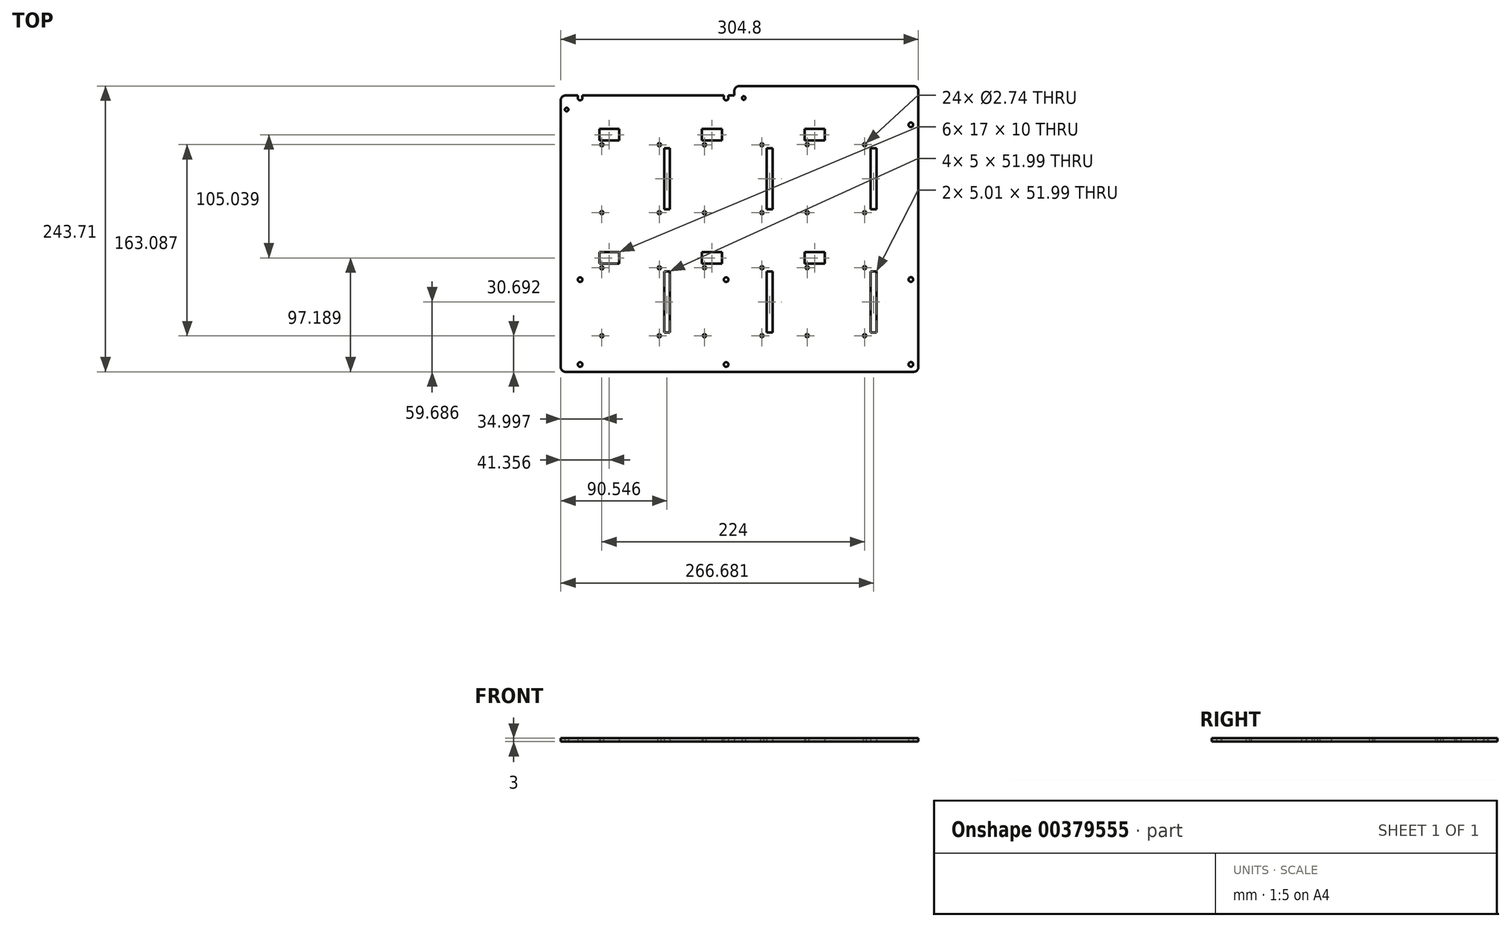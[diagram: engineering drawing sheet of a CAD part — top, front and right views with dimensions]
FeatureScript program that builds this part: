
annotation { "Feature Type Name" : "Feature", "Feature Type Description" : "" }
export const myFeature = defineFeature(function(context is Context, id is Id, definition is map)
    precondition{}
    {
        {
            var Q0;
            Q0=qCreatedBy(makeId("Top.planeOp"),FACE);
            var sketch = newSketch(context, id + "F0", { "sketchPlane" : qUnion([Q0])});
            skLineSegment(sketch, "E0.bottom", {"start": v(-157.61, -121.94) * mm, "end": v(139.26, -121.94) * mm});
            skLineSegment(sketch, "E0.top", {"start": v(-157.61, 121.77) * mm, "end": v(-156.57, 121.77) * mm});
            skLineSegment(sketch, "E0.left", {"start": v(-161.57, -117.98) * mm, "end": v(-161.57, 109.8) * mm});
            skLineSegment(sketch, "E0.right", {"start": v(143.23, -117.98) * mm, "end": v(143.23, 117.8) * mm});
            skArc(sketch, "E1", {"start": v(-147.04, 111.6) * mm, "mid": v(-145.06, 109.63) * mm, "end": v(-143.08, 111.6) * mm});
            skCircle(sketch, "E2", {"center": v(-145.06, -115.72) * mm, "radius": 1.98 * mm});
            skCircle(sketch, "E3", {"center": v(-145.06, -43.33) * mm, "radius": 1.98 * mm});
            skCircle(sketch, "E4", {"center": v(-20.6, -115.72) * mm, "radius": 1.98 * mm});
            skArc(sketch, "E5", {"start": v(-22.58, 111.6) * mm, "mid": v(-20.6, 109.63) * mm, "end": v(-18.62, 111.6) * mm});
            skCircle(sketch, "E6", {"center": v(136.88, 88.75) * mm, "radius": 1.98 * mm});
            skCircle(sketch, "E7", {"center": v(136.88, -115.6) * mm, "radius": 1.98 * mm});
            skCircle(sketch, "E8", {"center": v(136.88, -43.2) * mm, "radius": 1.98 * mm});
            skPoint(sketch, "E9.visualSharp", {"position": v(-161.57, 121.77) * mm});
            skPoint(sketch, "E10.visualSharp", {"position": v(-161.57, -121.94) * mm});
            skArc(sketch, "E10.filletArc", {"start": v(-161.57, -117.98) * mm, "mid": v(-160.41, -120.78) * mm, "end": v(-157.61, -121.94) * mm});
            skPoint(sketch, "E11.visualSharp", {"position": v(143.23, -121.94) * mm});
            skArc(sketch, "E11.filletArc", {"start": v(139.26, -121.94) * mm, "mid": v(142.07, -120.78) * mm, "end": v(143.23, -117.98) * mm});
            skPoint(sketch, "E12.visualSharp", {"position": v(143.23, 121.77) * mm});
            skArc(sketch, "E12.filletArc", {"start": v(143.23, 117.8) * mm, "mid": v(142.07, 120.6) * mm, "end": v(139.26, 121.77) * mm});
            skCircle(sketch, "E13.MirrorC", {"center": v(-77.58, 13.8) * mm, "radius": 1.37 * mm});
            skCircle(sketch, "E14.MirrorC", {"center": v(-126.57, 71.78) * mm, "radius": 1.37 * mm});
            skCircle(sketch, "E15.MirrorC", {"center": v(-126.57, 13.8) * mm, "radius": 1.37 * mm});
            skCircle(sketch, "E16.MirrorC", {"center": v(-77.58, 71.78) * mm, "radius": 1.37 * mm});
            skCircle(sketch, "E17.MirrorC", {"center": v(-77.58, -91.25) * mm, "radius": 1.37 * mm});
            skCircle(sketch, "E18.MirrorC", {"center": v(-126.57, -33.26) * mm, "radius": 1.37 * mm});
            skCircle(sketch, "E19.MirrorC", {"center": v(-77.58, -33.26) * mm, "radius": 1.37 * mm});
            skCircle(sketch, "E20.MirrorC", {"center": v(-126.57, -91.25) * mm, "radius": 1.37 * mm});
            skCircle(sketch, "E21.MirrorC", {"center": v(9.93, 13.75) * mm, "radius": 1.37 * mm});
            skCircle(sketch, "E22.MirrorC", {"center": v(-39.07, 71.73) * mm, "radius": 1.37 * mm});
            skCircle(sketch, "E23.MirrorC", {"center": v(-39.07, 13.75) * mm, "radius": 1.37 * mm});
            skCircle(sketch, "E24.MirrorC", {"center": v(9.93, 71.73) * mm, "radius": 1.37 * mm});
            skCircle(sketch, "E25.MirrorC", {"center": v(9.93, -91.12) * mm, "radius": 1.37 * mm});
            skCircle(sketch, "E26.MirrorC", {"center": v(-39.07, -33.14) * mm, "radius": 1.37 * mm});
            skCircle(sketch, "E27.MirrorC", {"center": v(9.93, -33.14) * mm, "radius": 1.37 * mm});
            skCircle(sketch, "E28.MirrorC", {"center": v(-39.07, -91.12) * mm, "radius": 1.37 * mm});
            skCircle(sketch, "E29.MirrorC", {"center": v(97.43, 13.85) * mm, "radius": 1.37 * mm});
            skCircle(sketch, "E30.MirrorC", {"center": v(48.43, 71.84) * mm, "radius": 1.37 * mm});
            skCircle(sketch, "E31.MirrorC", {"center": v(48.43, 13.85) * mm, "radius": 1.37 * mm});
            skCircle(sketch, "E32.MirrorC", {"center": v(97.43, 71.84) * mm, "radius": 1.37 * mm});
            skCircle(sketch, "E33.MirrorC", {"center": v(97.43, -91.1) * mm, "radius": 1.37 * mm});
            skCircle(sketch, "E34.MirrorC", {"center": v(48.43, -33.12) * mm, "radius": 1.37 * mm});
            skCircle(sketch, "E35.MirrorC", {"center": v(97.43, -33.12) * mm, "radius": 1.37 * mm});
            skCircle(sketch, "E36.MirrorC", {"center": v(48.43, -91.1) * mm, "radius": 1.37 * mm});
            skLineSegment(sketch, "E37.bottom", {"start": v(-128.71, -19.75) * mm, "end": v(-111.71, -19.75) * mm});
            skLineSegment(sketch, "E37.top", {"start": v(-128.71, -29.75) * mm, "end": v(-111.71, -29.75) * mm});
            skLineSegment(sketch, "E37.left", {"start": v(-128.71, -19.75) * mm, "end": v(-128.71, -29.75) * mm});
            skLineSegment(sketch, "E37.right", {"start": v(-41.2, -19.75) * mm, "end": v(-41.2, -29.75) * mm});
            skLineSegment(sketch, "E38.MirrorCS", {"start": v(-24.2, -19.75) * mm, "end": v(-24.2, -29.75) * mm});
            skLineSegment(sketch, "E39.MirrorCS", {"start": v(-24.2, -29.75) * mm, "end": v(-41.2, -29.75) * mm});
            skLineSegment(sketch, "E40.MirrorCS", {"start": v(-24.2, -19.75) * mm, "end": v(-41.2, -19.75) * mm});
            skLineSegment(sketch, "E41", {"start": v(-111.71, -19.75) * mm, "end": v(-111.71, -29.75) * mm});
            skLineSegment(sketch, "E42.right", {"start": v(46.3, -19.75) * mm, "end": v(46.3, -29.75) * mm});
            skLineSegment(sketch, "E43.MirrorCS", {"start": v(63.3, -19.75) * mm, "end": v(63.3, -29.75) * mm});
            skLineSegment(sketch, "E44.MirrorCS", {"start": v(63.3, -29.75) * mm, "end": v(46.3, -29.75) * mm});
            skLineSegment(sketch, "E45.MirrorCS", {"start": v(63.3, -19.75) * mm, "end": v(46.3, -19.75) * mm});
            skLineSegment(sketch, "E46.bottom", {"start": v(-73.52, 68.78) * mm, "end": v(-68.52, 68.78) * mm});
            skLineSegment(sketch, "E46.top", {"start": v(-73.52, 16.8) * mm, "end": v(-68.52, 16.8) * mm});
            skLineSegment(sketch, "E46.left", {"start": v(-73.52, 68.78) * mm, "end": v(-73.52, 16.8) * mm});
            skLineSegment(sketch, "E46.right", {"start": v(-68.52, 68.78) * mm, "end": v(-68.52, 16.8) * mm});
            skLineSegment(sketch, "E47.bottom", {"start": v(13.98, 68.78) * mm, "end": v(18.98, 68.78) * mm});
            skLineSegment(sketch, "E47.top", {"start": v(13.98, 16.8) * mm, "end": v(18.98, 16.8) * mm});
            skLineSegment(sketch, "E47.left", {"start": v(13.98, 68.78) * mm, "end": v(13.98, 16.8) * mm});
            skLineSegment(sketch, "E47.right", {"start": v(18.98, 68.78) * mm, "end": v(18.98, 16.8) * mm});
            skLineSegment(sketch, "E48.bottom", {"start": v(102.6, 68.78) * mm, "end": v(107.61, 68.78) * mm});
            skLineSegment(sketch, "E48.top", {"start": v(102.6, 16.8) * mm, "end": v(107.61, 16.8) * mm});
            skLineSegment(sketch, "E48.left", {"start": v(102.6, 68.78) * mm, "end": v(102.6, 16.8) * mm});
            skLineSegment(sketch, "E48.right", {"start": v(107.61, 68.78) * mm, "end": v(107.61, 16.8) * mm});
            skLineSegment(sketch, "E49.bottom", {"start": v(-73.52, -36.26) * mm, "end": v(-68.52, -36.26) * mm});
            skLineSegment(sketch, "E49.top", {"start": v(-73.52, -88.25) * mm, "end": v(-68.52, -88.25) * mm});
            skLineSegment(sketch, "E49.left", {"start": v(-73.52, -36.26) * mm, "end": v(-73.52, -88.25) * mm});
            skLineSegment(sketch, "E49.right", {"start": v(-68.52, -36.26) * mm, "end": v(-68.52, -88.25) * mm});
            skLineSegment(sketch, "E50.bottom", {"start": v(13.98, -36.26) * mm, "end": v(18.98, -36.26) * mm});
            skLineSegment(sketch, "E50.top", {"start": v(13.98, -88.25) * mm, "end": v(18.98, -88.25) * mm});
            skLineSegment(sketch, "E50.left", {"start": v(13.98, -36.26) * mm, "end": v(13.98, -88.25) * mm});
            skLineSegment(sketch, "E50.right", {"start": v(18.98, -36.26) * mm, "end": v(18.98, -88.25) * mm});
            skLineSegment(sketch, "E51.bottom", {"start": v(102.6, -36.26) * mm, "end": v(107.61, -36.26) * mm});
            skLineSegment(sketch, "E51.top", {"start": v(102.6, -88.25) * mm, "end": v(107.61, -88.25) * mm});
            skLineSegment(sketch, "E51.left", {"start": v(102.6, -36.26) * mm, "end": v(102.6, -88.25) * mm});
            skLineSegment(sketch, "E51.right", {"start": v(107.61, -36.26) * mm, "end": v(107.61, -88.25) * mm});
            skLineSegment(sketch, "E52", {"start": v(-242.67, -151.94) * mm, "end": v(205.36, -151.94) * mm, "construction": true});
            skCircle(sketch, "E53.MirrorC", {"center": v(-20.6, -43.33) * mm, "radius": 1.98 * mm});
            skLineSegment(sketch, "E54", {"start": v(-171.72, 113.77) * mm, "end": v(-147.04, 113.77) * mm, "construction": true});
            skLineSegment(sketch, "E55", {"start": v(-13.6, 137.69) * mm, "end": v(-13.6, 102.93) * mm, "construction": true});
            skLineSegment(sketch, "E56", {"start": v(-169.38, 111.6) * mm, "end": v(164.1, 111.6) * mm, "construction": true});
            skLineSegment(sketch, "E57", {"start": v(-5.6, 125.2) * mm, "end": v(-5.6, 95.42) * mm, "construction": true});
            skCircle(sketch, "E58", {"center": v(-5.6, 111.6) * mm, "radius": 1.5 * mm});
            skLineSegment(sketch, "E59", {"start": v(-156.57, 127.39) * mm, "end": v(-156.57, 85.38) * mm, "construction": true});
            skLineSegment(sketch, "E60", {"start": v(-167.89, 101.77) * mm, "end": v(-140.58, 101.77) * mm, "construction": true});
            skCircle(sketch, "E61", {"center": v(-156.57, 101.77) * mm, "radius": 1.5 * mm});
            skLineSegment(sketch, "E62", {"start": v(-157.61, 113.77) * mm, "end": v(-147.04, 113.77) * mm});
            skLineSegment(sketch, "E63", {"start": v(-13.6, 117.8) * mm, "end": v(-13.6, 117.8) * mm});
            skLineSegment(sketch, "E64.trimOffspring", {"start": v(-9.64, 121.77) * mm, "end": v(139.26, 121.77) * mm});
            skPoint(sketch, "E65.visualSharp", {"position": v(-161.57, 113.77) * mm});
            skArc(sketch, "E65.filletArc", {"start": v(-157.61, 113.77) * mm, "mid": v(-160.41, 112.6) * mm, "end": v(-161.57, 109.8) * mm});
            skPoint(sketch, "E66.visualSharp", {"position": v(-13.6, 121.77) * mm});
            skArc(sketch, "E66.filletArc", {"start": v(-9.64, 121.77) * mm, "mid": v(-12.44, 120.6) * mm, "end": v(-13.6, 117.8) * mm});
            skPoint(sketch, "E67.visualSharp", {"position": v(-13.6, 113.77) * mm});
            skLineSegment(sketch, "E68", {"start": v(-147.04, 111.6) * mm, "end": v(-147.04, 113.77) * mm});
            skLineSegment(sketch, "E69", {"start": v(-143.08, 111.6) * mm, "end": v(-143.08, 113.77) * mm});
            skLineSegment(sketch, "E70.trimOffspring", {"start": v(-143.08, 113.77) * mm, "end": v(-22.58, 113.77) * mm, "construction": true});
            skLineSegment(sketch, "E71.trimOffspring", {"start": v(-143.08, 113.77) * mm, "end": v(-22.58, 113.77) * mm});
            skLineSegment(sketch, "E72", {"start": v(-22.58, 111.6) * mm, "end": v(-22.58, 113.77) * mm});
            skLineSegment(sketch, "E73", {"start": v(-18.62, 111.6) * mm, "end": v(-18.62, 113.77) * mm});
            skLineSegment(sketch, "E74.trimOffspring", {"start": v(-18.62, 113.77) * mm, "end": v(4.41, 113.77) * mm, "construction": true});
            skLineSegment(sketch, "E75.trimOffspring", {"start": v(-18.62, 113.77) * mm, "end": v(-13.6, 113.77) * mm});
            skLineSegment(sketch, "E76", {"start": v(-13.6, 113.77) * mm, "end": v(-13.6, 113.77) * mm});
            skLineSegment(sketch, "E77", {"start": v(-13.6, 113.77) * mm, "end": v(-13.6, 117.8) * mm});
            skLineSegment(sketch, "E78", {"start": v(-128.71, -39.97) * mm, "end": v(-128.71, 87.75) * mm, "construction": true});
            skLineSegment(sketch, "E79", {"start": v(-139.94, 75.29) * mm, "end": v(76.7, 75.29) * mm, "construction": true});
            skLineSegment(sketch, "E80", {"start": v(-41.2, -39.58) * mm, "end": v(-41.2, 88.8) * mm, "construction": true});
            skLineSegment(sketch, "E81", {"start": v(46.3, -38.27) * mm, "end": v(46.3, 88.27) * mm, "construction": true});
            skLineSegment(sketch, "E82.bottom", {"start": v(-128.71, 85.29) * mm, "end": v(-111.71, 85.29) * mm});
            skLineSegment(sketch, "E82.top", {"start": v(-128.71, 75.29) * mm, "end": v(-111.71, 75.29) * mm});
            skLineSegment(sketch, "E82.left", {"start": v(-128.71, 85.29) * mm, "end": v(-128.71, 75.29) * mm});
            skLineSegment(sketch, "E83", {"start": v(-111.71, 85.29) * mm, "end": v(-111.71, 75.29) * mm});
            skLineSegment(sketch, "E84.bottom", {"start": v(-41.2, 85.29) * mm, "end": v(-24.2, 85.29) * mm});
            skLineSegment(sketch, "E84.top", {"start": v(-41.2, 75.29) * mm, "end": v(-24.2, 75.29) * mm});
            skLineSegment(sketch, "E84.left", {"start": v(-41.2, 85.29) * mm, "end": v(-41.2, 75.29) * mm});
            skLineSegment(sketch, "E85", {"start": v(-24.2, 85.29) * mm, "end": v(-24.2, 75.29) * mm});
            skLineSegment(sketch, "E86.bottom", {"start": v(46.3, 85.29) * mm, "end": v(63.3, 85.29) * mm});
            skLineSegment(sketch, "E86.top", {"start": v(46.3, 75.29) * mm, "end": v(63.3, 75.29) * mm});
            skLineSegment(sketch, "E86.left", {"start": v(46.3, 85.29) * mm, "end": v(46.3, 75.29) * mm});
            skLineSegment(sketch, "E87", {"start": v(63.3, 85.29) * mm, "end": v(63.3, 75.29) * mm});
            skSolve(sketch);
        }
        {
            var Q0;
            Q0=makeQuery(id+"F0.imprint","IMPRINT",FACE,{"disambiguationData":[TD([[makeQuery(id+"F0.imprint","IMPRINT",EDGE,{"derivedFrom":sQuery(id+"F0.wireOp",EDGE,"E0.bottom")}),1.0]])]});
            extrude(context, id + "F1", {"entities" : qUnion([Q0]), "depth" : 3 * mm});
        }
    });
